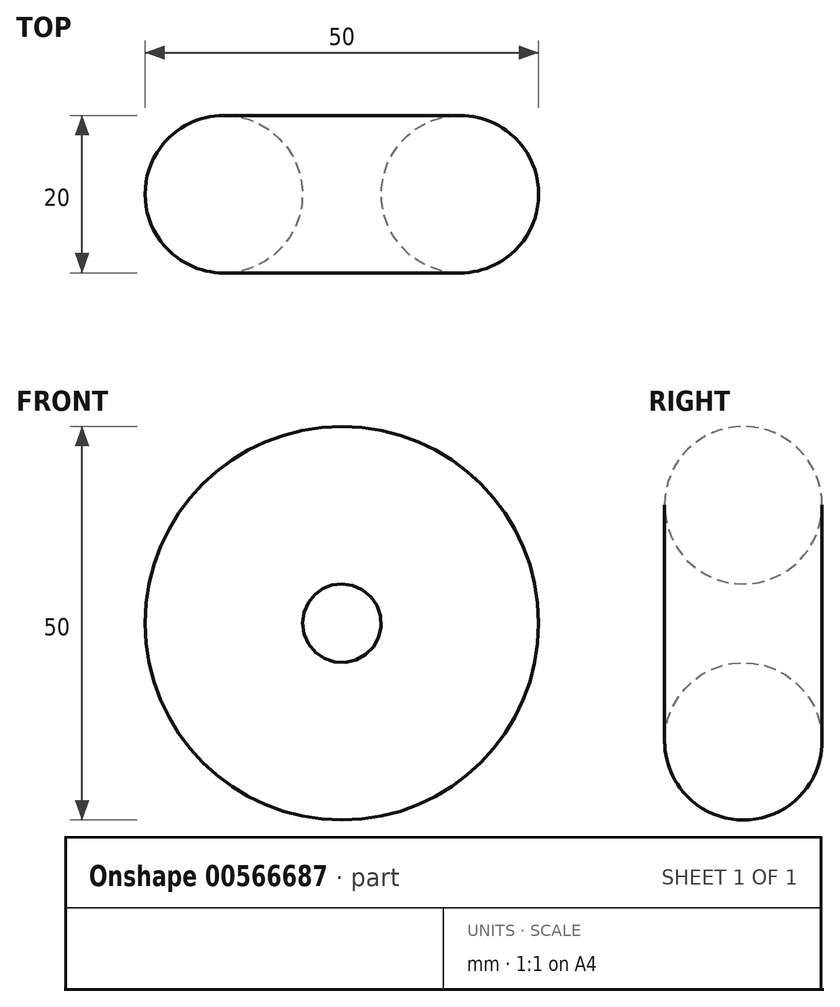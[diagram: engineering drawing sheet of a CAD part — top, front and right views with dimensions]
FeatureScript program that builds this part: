
annotation { "Feature Type Name" : "Feature", "Feature Type Description" : "" }
export const myFeature = defineFeature(function(context is Context, id is Id, definition is map)
    precondition{}
    {
        {
            var Q0;
            Q0=qCreatedBy(makeId("Top.planeOp"),FACE);
            var sketch = newSketch(context, id + "F0", { "sketchPlane" : qUnion([Q0])});
            skLineSegment(sketch, "E0", {"start": v(0, 0) * mm, "end": v(15, 0) * mm});
            skCircle(sketch, "E1", {"center": v(15, 0) * mm, "radius": 10 * mm});
            skSolve(sketch);
        }
        {
            var Q0;
            Q0=qCreatedBy(makeId("Top.planeOp"),FACE);
            var sketch = newSketch(context, id + "F1", { "sketchPlane" : qUnion([Q0])});
            skLineSegment(sketch, "E2", {"start": v(0, 26.67) * mm, "end": v(0, -27.17) * mm, "construction": true});
            skSolve(sketch);
        }
        {
            var Q0;
            Q0=makeQuery(id+"F0.imprint","IMPRINT",FACE,{"disambiguationData":[TD([[makeQuery(id+"F0.imprint","IMPRINT",EDGE,{"derivedFrom":sQuery(id+"F0.wireOp",EDGE,"E1")}),1.0]])]});
            var Q1;
            Q1=sQuery(id+"F1.wireOp",EDGE,"E2");
            revolve(context, id + "F2", {"entities" : qUnion([Q0]), "axis" : qUnion([Q1]), "revolveType" : RevolveType.SYMMETRIC, "angle" : 360 * degree});
        }
    });
